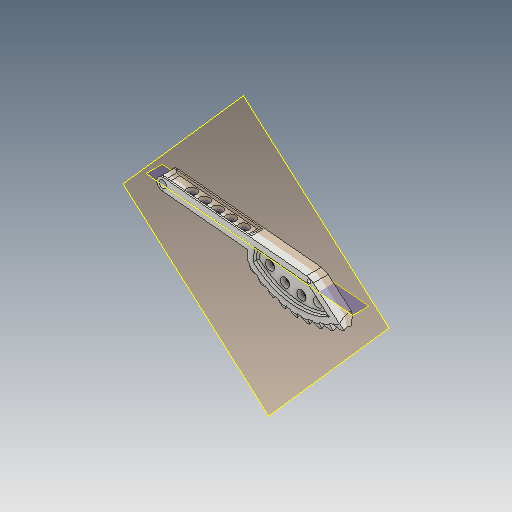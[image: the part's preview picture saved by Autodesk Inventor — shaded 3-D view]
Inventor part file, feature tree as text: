
AUTODESK INVENTOR PART (.ipt)
format: ipt  version: 2020.3 (Build 243373010, 373A)  size: 616,448 bytes
history: native  units: mm
features: other x17, sketch x10, plane x2
ambient origin geometry x8: Origin, YZ Plane, XZ Plane, XY Plane, X Axis, Y Axis, Z Axis, Center Point
bodies: Solid1 (feature_tree)
feature tree (29):
  other  "Worm Gear"
  other  "Solid1::Worm Gear"
  other  "TaggingFeature1"
  other  "Base Body Sketch"
  sketch  "Sketch8"  dims[d0=10.0mm]
  other  "Tooth Sketch"
  sketch  "Sketch9"  dims[d68=138.0mm d69=0.0mm d73=0.0mm d80=0.0mm d81=0.0mm d82=0.0mm d84=0.0mm d86=138.0mm]
  sketch  "Sketch12"
  sketch  "Sketch13"
  sketch  "Sketch14"
  sketch  "Sketch15"
  sketch  "Sketch16"
  sketch  "Sketch17"
  sketch  "Sketch18"
  sketch  "Sketch19"
  plane  "YZ Plane_1"
  plane  "XY Plane_1"
  other  "Tooth Plane"
  other  "Z Axis_1"
  other  "Center Point_1"
  other  "Srf1"
  other  "Srf1::Derived"
  other  "Position iMate"
  other  "Mesh iMate"
  other  "Align iMate"
  other  "Start plane iMate"
  other  "Axis iMate"
  other  "Center Distance iMate"
  other  "Mesh iMate2"
